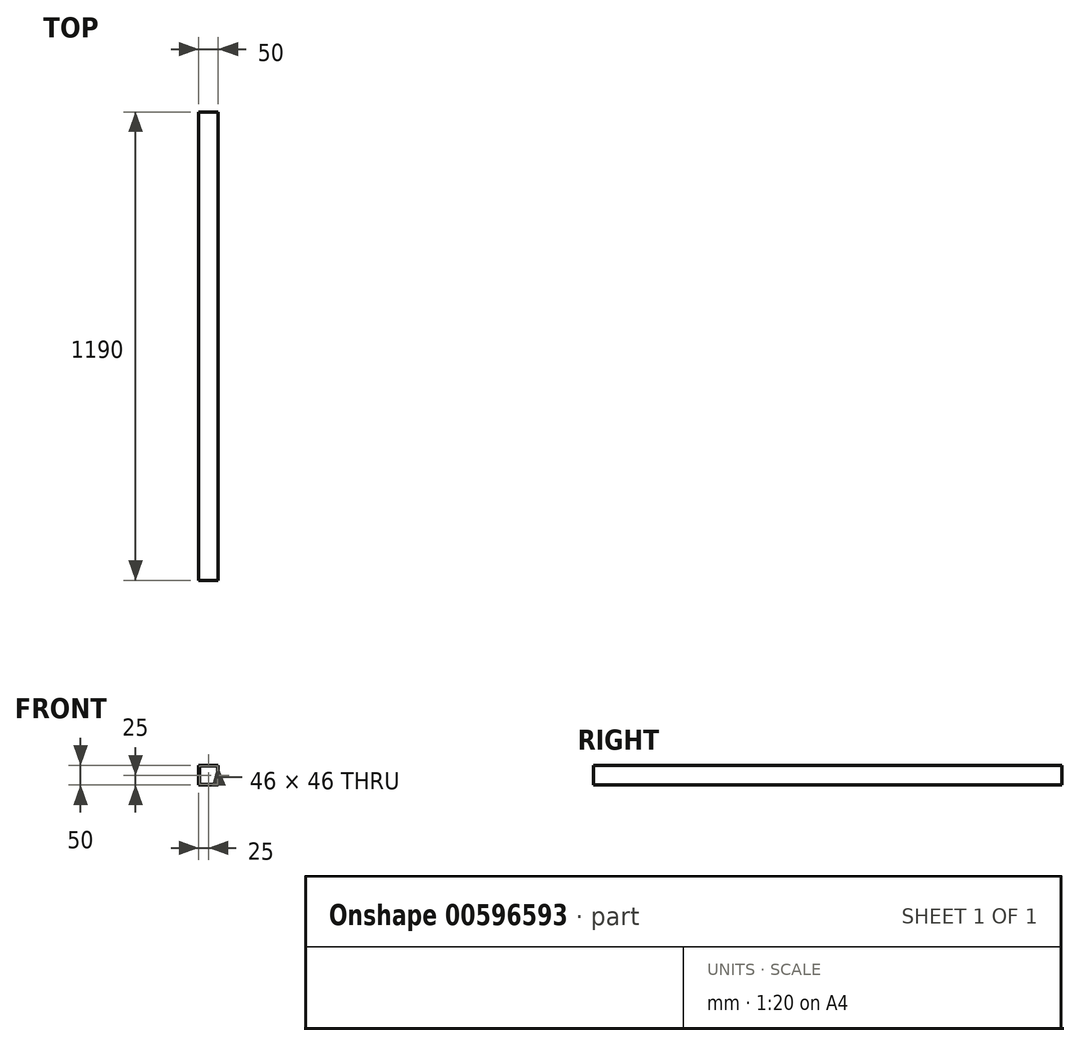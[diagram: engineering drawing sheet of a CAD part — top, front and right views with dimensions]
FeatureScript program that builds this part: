
annotation { "Feature Type Name" : "Feature", "Feature Type Description" : "" }
export const myFeature = defineFeature(function(context is Context, id is Id, definition is map)
    precondition{}
    {
        {
            var Q0;
            Q0=qCreatedBy(makeId("Front.planeOp"),FACE);
            var sketch = newSketch(context, id + "F0", { "sketchPlane" : qUnion([Q0])});
            skLineSegment(sketch, "E0.bottom", {"start": v(0, 0) * mm, "end": v(50, 0) * mm});
            skLineSegment(sketch, "E0.top", {"start": v(0, 50) * mm, "end": v(50, 50) * mm});
            skLineSegment(sketch, "E0.left", {"start": v(0, 0) * mm, "end": v(0, 50) * mm});
            skLineSegment(sketch, "E0.right", {"start": v(50, 0) * mm, "end": v(50, 50) * mm});
            skLineSegment(sketch, "E1.bottom", {"start": v(2, 2) * mm, "end": v(48, 2) * mm});
            skLineSegment(sketch, "E1.top", {"start": v(2, 48) * mm, "end": v(48, 48) * mm});
            skLineSegment(sketch, "E1.left", {"start": v(2, 2) * mm, "end": v(2, 48) * mm});
            skLineSegment(sketch, "E1.right", {"start": v(48, 2) * mm, "end": v(48, 48) * mm});
            skSolve(sketch);
        }
        {
            var Q0;
            Q0 = qSketchRegion(id + "F0", true);
            extrude(context, id + "F1", {"entities" : qUnion([Q0]), "depth" : 1190 * mm, "offsetDistance" : 25 * mm});
        }
    });
